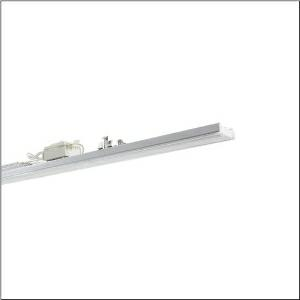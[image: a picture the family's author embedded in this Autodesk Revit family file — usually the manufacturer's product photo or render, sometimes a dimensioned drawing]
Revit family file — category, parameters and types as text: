
# Revit family: licross_r__21_recessed_mo_52te12dn465g_9b7f
name_source: partatom
category: Lighting Fixtures
units: mm (PartAtom-declared; Revit-internal decimal feet)

## family parameters
Cut with Voids When Loaded = No
Host = Face
Light Source = No
Part Type = Normal
Room Calculation Point = No
Round Connector Dimension = Use Diameter
Shared = No

## types (1)
- --- (1 x LED, 6590 lm, 36.3 W, 4000K)
    Apparent Load = 36 VA
    CIE Flux Codes = 72 92 99 100 100
    Color Rendering = 80
    Color Temperature = 4000K
    Default Elevation = 1800 mm
    Description = Licross® 21 Recessed MO, luminaire insert, of sheet steel, galvanised, coil coated, white, length: 1.500mm, width: 66mm, height: 67mm, LED rated luminous flux: 6.590lm, light colour: 840, control gear: DALI 2, with plug, 5-pole, with phase selection, mains connection: 220..240V, AC, 50/60Hz, rated input power: 36W, internal wiring halogen-free, primary optical cover: cover, of PMMA, light emission: direct distribution, primary light characteristic: symmetric, protection rating (complete): IP54, insulation class (complete): insulation class I (protective earthing), certification: CE, ENEC, VDE, UKCA, protection symbol: D if used in an environment with non-conductive dust loads with corresponding accessories, impact resistance: IK06, permissible ambient temperature for indoor applications: -25..+40°C, corresponds to IFS (International Featured Standards) requirements for safety and quality in the food industry, reducing of maximum allowable ambient temperature of 5°C with ceiling mounting, LABS conformity tested according to VDMA 24364:2018-05, packaging unit: 1 piece
    Height = 58 mm
    Lamp = 1 x LED
    Lamp Light Flux = 6590 lm
    Lamp Power = 36.3 W
    Lamp count = 1
    Length = 1500 mm
    Luminous efficacy = 182 lm/W
    Manufacturer = Siteco
    ModVariant = No
    Model = 52TE12DN465G
    Mounting Place = Ceiling
    Mounting Type = Pendant
    Number of Poles = 1
    OnlyDefault = Yes
    Power Factor = 1
    Product Name = Licross® 21 Recessed MO
    Product group = luminaire insert | ceiling pendant
    ProductGroupID = 902
    Protection Class = Protection class I
    Protection Degree = IP 54
    RLX_Detail_Level = 1
    RLX_Emergency_Light_Flux = 0 lm
    RLX_Emergency_Type = 0
    RLX_Emergency_Type_DB = No
    RlxData = <blob elided: 24653 chars, md5=c8b020b1>
    Socket = socket
    Standby Power = 0 W
    System Light Flux = 6590 lm
    System Power = 36 W
    Type Comments = factory setting: luminous flux: 100 % | dim-lin: 254 | 242 mA
    Type Image = l_1296930.jpg
    URL = http://relux.com
    VarID = @adj_101335
    Voltage = 0 V
    Weight = 0.00 kg
    Width = 66 mm

## geometry (parser evidence)
native form markers: Blend x4, Sweep x14
no freeform markers — native parametric forms only
